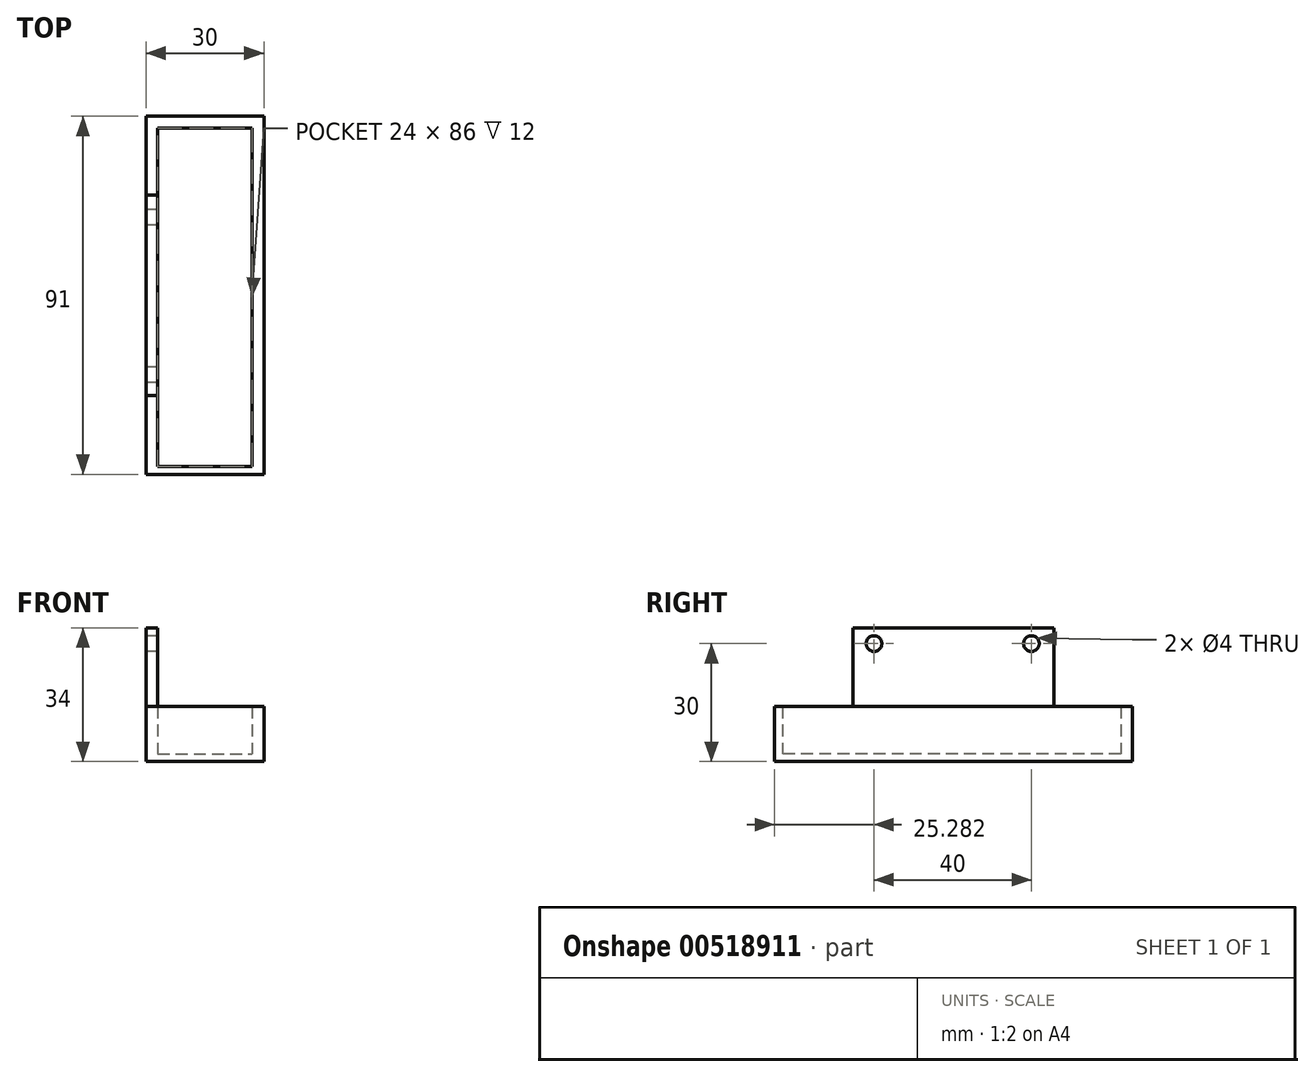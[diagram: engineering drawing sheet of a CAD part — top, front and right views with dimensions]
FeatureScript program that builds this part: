
annotation { "Feature Type Name" : "Feature", "Feature Type Description" : "" }
export const myFeature = defineFeature(function(context is Context, id is Id, definition is map)
    precondition{}
    {
        {
            var Q0;
            Q0=qCreatedBy(makeId("Top.planeOp"),FACE);
            var sketch = newSketch(context, id + "F0", { "sketchPlane" : qUnion([Q0])});
            skLineSegment(sketch, "E0.bottom", {"start": v(-12.54, 45.8) * mm, "end": v(17.46, 45.8) * mm});
            skLineSegment(sketch, "E0.top", {"start": v(-12.54, -45.2) * mm, "end": v(17.46, -45.2) * mm});
            skLineSegment(sketch, "E0.left", {"start": v(-12.54, 45.8) * mm, "end": v(-12.54, -45.2) * mm});
            skLineSegment(sketch, "E0.right", {"start": v(17.46, 45.8) * mm, "end": v(17.46, -45.2) * mm});
            skSolve(sketch);
        }
        {
            var Q0;
            Q0=makeQuery(id+"F0.imprint","IMPRINT",FACE,{"disambiguationData":[TD([[makeQuery(id+"F0.imprint","IMPRINT",EDGE,{"derivedFrom":sQuery(id+"F0.wireOp",EDGE,"E0.bottom")}),-1.0]])]});
            extrude(context, id + "F1", {"entities" : qUnion([Q0]), "depth" : 2 * mm, "offsetDistance" : 25 * mm});
        }
        {
            var Q0;
            Q0=makeQuery(id+"F1.opExtrude","CAP_FACE",FACE,{"disambiguationData":[OSD([sQuery(id+"F0.wireOp",EDGE,"E0.bottom"),sQuery(id+"F0.wireOp",EDGE,"E0.top"),sQuery(id+"F0.wireOp",EDGE,"E0.left"),sQuery(id+"F0.wireOp",EDGE,"E0.right")])],"isStart":false});
            var sketch = newSketch(context, id + "F2", { "sketchPlane" : qUnion([Q0])});
            skLineSegment(sketch, "E1.bottom", {"start": v(-12.54, 45.8) * mm, "end": v(17.46, 45.8) * mm});
            skLineSegment(sketch, "E1.top", {"start": v(-12.54, -45.2) * mm, "end": v(17.46, -45.2) * mm});
            skLineSegment(sketch, "E1.left", {"start": v(-12.54, 45.8) * mm, "end": v(-12.54, -45.2) * mm});
            skLineSegment(sketch, "E1.right", {"start": v(17.46, 45.8) * mm, "end": v(17.46, -45.2) * mm});
            skLineSegment(sketch, "E2.bottom", {"start": v(-9.54, 42.8) * mm, "end": v(14.46, 42.8) * mm});
            skLineSegment(sketch, "E2.top", {"start": v(-9.54, -43.2) * mm, "end": v(14.46, -43.2) * mm});
            skLineSegment(sketch, "E2.left", {"start": v(-9.54, 42.8) * mm, "end": v(-9.54, -43.2) * mm});
            skLineSegment(sketch, "E2.right", {"start": v(14.46, 42.8) * mm, "end": v(14.46, -43.2) * mm});
            skSolve(sketch);
        }
        {
            var Q0;
            Q0 = qSketchRegion(id + "F2", true);
            extrude(context, id + "F3", {"entities" : qUnion([Q0]), "operationType" : NewBodyOperationType.ADD, "depth" : 32 * mm, "offsetDistance" : 25 * mm});
        }
        {
            var Q0;
            Q0=makeQuery(id+"F3.boolean.opBoolean","MERGE",FACE,{"derivedFrom":[makeQuery(id+"F1.opExtrude","SWEPT_FACE",FACE,{"disambiguationData":[OSD([sQuery(id+"F0.wireOp",EDGE,"E0.left")])]}),makeQuery(id+"F3.opExtrude","SWEPT_FACE",FACE,{"disambiguationData":[OSD([sQuery(id+"F2.wireOp",EDGE,"E1.left")])]})]});
            var sketch = newSketch(context, id + "F4", { "sketchPlane" : qUnion([Q0])});
            skCircle(sketch, "E3", {"center": v(-20.1, 30) * mm, "radius": 2 * mm});
            skCircle(sketch, "E4", {"center": v(19.9, 30) * mm, "radius": 2 * mm});
            skSolve(sketch);
        }
        {
            var Q0;
            Q0 = qSketchRegion(id + "F4", true);
            extrude(context, id + "F5", {"entities" : qUnion([Q0]), "operationType" : NewBodyOperationType.REMOVE, "oppositeDirection" : true, "depth" : 25 * mm, "offsetDistance" : 25 * mm});
        }
        {
            var Q0;
            Q0=makeQuery(id+"F3.opExtrude","CAP_FACE",FACE,{"disambiguationData":[OSD([sQuery(id+"F2.wireOp",EDGE,"E1.bottom"),sQuery(id+"F2.wireOp",EDGE,"E1.top"),sQuery(id+"F2.wireOp",EDGE,"E1.left"),sQuery(id+"F2.wireOp",EDGE,"E1.right"),sQuery(id+"F2.wireOp",EDGE,"E2.bottom"),sQuery(id+"F2.wireOp",EDGE,"E2.top"),sQuery(id+"F2.wireOp",EDGE,"E2.left"),sQuery(id+"F2.wireOp",EDGE,"E2.right")])],"isStart":false});
            var sketch = newSketch(context, id + "F6", { "sketchPlane" : qUnion([Q0])});
            skLineSegment(sketch, "E5", {"start": v(-12.54, 25.8) * mm, "end": v(-9.54, 25.8) * mm});
            skLineSegment(sketch, "E6", {"start": v(-9.54, 25.8) * mm, "end": v(-9.54, 42.8) * mm});
            skLineSegment(sketch, "E7", {"start": v(-9.54, 42.8) * mm, "end": v(14.46, 42.8) * mm});
            skLineSegment(sketch, "E8", {"start": v(14.46, 42.8) * mm, "end": v(14.46, -43.2) * mm});
            skLineSegment(sketch, "E9", {"start": v(14.46, -43.2) * mm, "end": v(-9.54, -43.2) * mm});
            skLineSegment(sketch, "E10", {"start": v(-9.54, -43.2) * mm, "end": v(-9.54, -25.2) * mm});
            skLineSegment(sketch, "E11", {"start": v(-9.54, -25.2) * mm, "end": v(-12.54, -25.2) * mm});
            skLineSegment(sketch, "E12", {"start": v(-12.54, -25.2) * mm, "end": v(-12.54, -45.2) * mm});
            skLineSegment(sketch, "E13", {"start": v(-12.54, -45.2) * mm, "end": v(17.46, -45.2) * mm});
            skLineSegment(sketch, "E14", {"start": v(17.46, -45.2) * mm, "end": v(17.46, 45.8) * mm});
            skLineSegment(sketch, "E15", {"start": v(17.46, 45.8) * mm, "end": v(-12.54, 45.8) * mm});
            skLineSegment(sketch, "E16", {"start": v(-12.54, 45.8) * mm, "end": v(-12.54, 25.8) * mm});
            skSolve(sketch);
        }
        {
            var Q0;
            Q0 = qSketchRegion(id + "F6", true);
            extrude(context, id + "F7", {"entities" : qUnion([Q0]), "operationType" : NewBodyOperationType.REMOVE, "oppositeDirection" : true, "depth" : 20 * mm, "offsetDistance" : 25 * mm});
        }
    });
